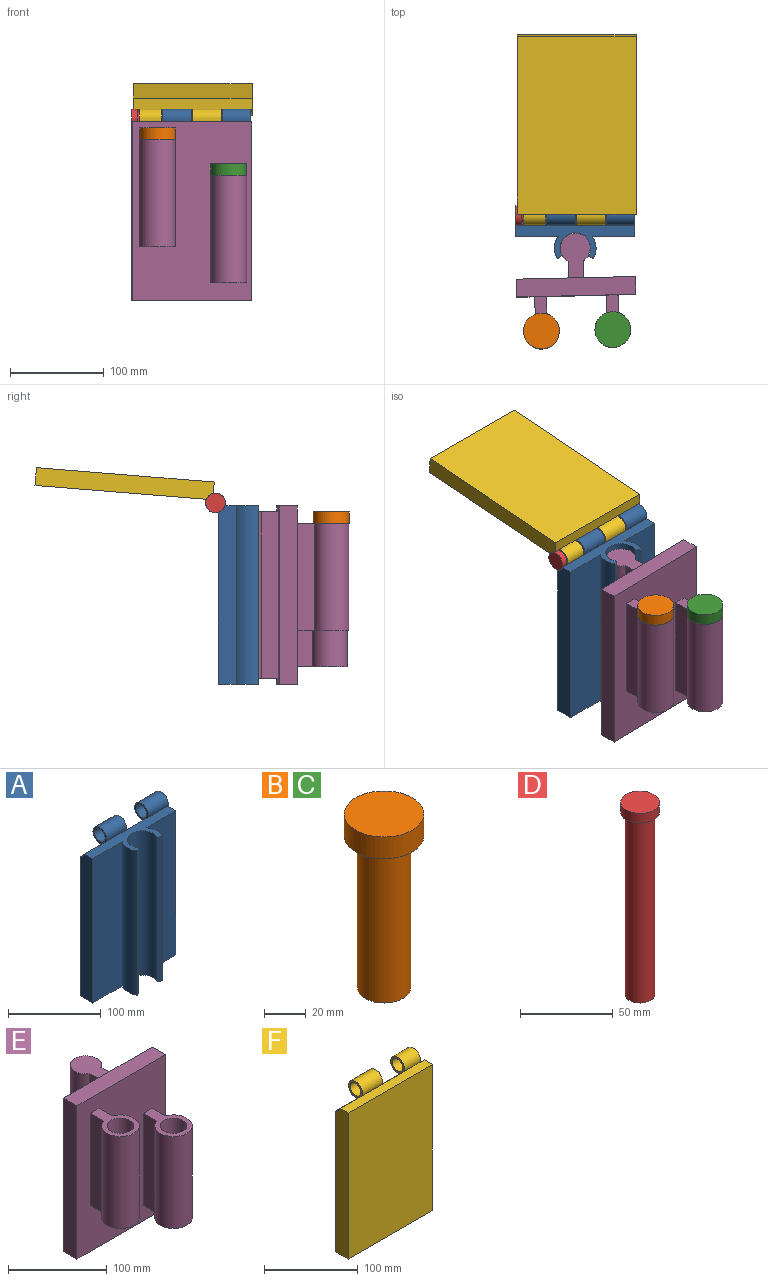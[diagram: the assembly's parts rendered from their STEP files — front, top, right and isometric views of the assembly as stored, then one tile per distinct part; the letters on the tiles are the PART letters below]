
ASSEMBLY  parts=6 mates=7
PART A: 21 faces, bbox 127x56.5x204.2 mm
  f0: cylinder r=10.48mm len=33.27mm, axis (1,0,0), area 333mm2, adj f3,f7,f17,f20
  f1: plane 190.5x45.26mm, normal (0,-1,0), area 8622.2mm2, adj f3,f4,f5,f10
  f2: plane 190.5x45.26mm, normal (0,-1,0), area 8622.2mm2, adj f3,f5,f6,f8
  f3: plane 127x36.05mm, normal (0,0,1), area 1790.7mm2, adj f0,f1,f2,f4,f6,f8,f9,f10
  f4: plane 190.5x19.05mm, normal (-1,0,0), area 3598.2mm2, adj f1,f3,f5,f7,f13
  f5: plane 127x42.86mm, normal (0,0,-1), area 2655.5mm2, adj f1,f2,f4,f6,f7,f8,f9,f10
  f6: plane 204.15x32.7mm, normal (1,0,0), area 3742mm2, adj f2,f3,f5,f7,f18,f19
  f7: plane 183.69x127mm, normal (0,1,0), area 23328.6mm2, adj f0,f4,f5,f6,f13,f15,f19
  f8: cylinder r=22.23mm len=190.5mm, axis (0,0,-1), area 4792.1mm2, adj f2,f3,f5,f9
  f9: plane 190.5x5.16mm, normal (-0.5,-0.87,0), area 1134.1mm2, adj f3,f5,f8,f12
  f10: cylinder r=22.23mm len=190.5mm, axis (0,0,-1), area 4792.1mm2, adj f1,f3,f5,f11
  f11: plane 190.5x5.16mm, normal (0.5,-0.87,0), area 1134.1mm2, adj f3,f5,f10,f12
  f12: cylinder r=16.27mm len=190.5mm, axis (0,0,-1), area 12984.4mm2, adj f3,f5,f9,f11
  f13: cylinder r=10.48mm len=33.27mm, axis (1,0,0), area 333mm2, adj f3,f4,f7,f16
  f14: cylinder r=8mm len=30.23mm, axis (1,0,0), area 1519.5mm2, adj f16,f17
  f15: cylinder r=10.48mm len=30.23mm, axis (1,0,0), area 1687.4mm2, adj f3,f7,f16,f17
  f16: plane 20.96x20.96mm, normal (-1,0,0), area 143.8mm2, adj f13,f14,f15
  f17: plane 20.96x20.96mm, normal (1,0,0), area 143.8mm2, adj f0,f14,f15
  f18: cylinder r=8mm len=30.23mm, axis (1,0,0), area 1519.5mm2, adj f6,f20
  f19: cylinder r=10.48mm len=30.23mm, axis (1,0,0), area 1687.4mm2, adj f3,f6,f7,f20
  f20: plane 20.96x20.96mm, normal (-1,0,0), area 143.8mm2, adj f0,f18,f19
PART B: 5 faces, bbox 38.1x38.1x101.6 mm
  f0: cylinder r=12.7mm len=88.9mm, axis (0,0,-1), area 7093.9mm2, adj f1,f4
  f1: plane 25.4x25.4mm, normal (0,0,-1), area 506.7mm2, adj f0
  f2: cylinder r=19.05mm len=38.1mm, axis (0,0,-1), area 1520.1mm2, adj f3,f4
  f3: plane 38.1x38.1mm, normal (0,0,1), area 1140.1mm2, adj f2
  f4: plane 38.1x38.1mm, normal (0,0,-1), area 633.4mm2, adj f0,f2
PART C: same geometry as B
PART D: 5 faces, bbox 21x21x127 mm
  f0: cylinder r=7.94mm len=120.65mm, axis (0,0,-1), area 6017.2mm2, adj f1,f4
  f1: plane 15.88x15.88mm, normal (0,0,-1), area 197.9mm2, adj f0
  f2: cylinder r=10.48mm len=20.96mm, axis (0,0,-1), area 418mm2, adj f3,f4
  f3: plane 20.96x20.96mm, normal (0,0,1), area 344.9mm2, adj f2
  f4: plane 20.96x20.96mm, normal (0,0,-1), area 146.9mm2, adj f0,f2
PART E: 23 faces, bbox 127x122.7x190.5 mm
  f0: plane 190.5x127mm, normal (0,-1,0), area 21290.3mm2, adj f1,f2,f3,f4,f7,f8,f10,f11
  f1: plane 190.5x19.05mm, normal (1,0,0), area 3629mm2, adj f0,f2,f4,f5
  f2: plane 127x19.05mm, normal (0,0,1), area 2419.3mm2, adj f0,f1,f3,f5
  f3: plane 190.5x19.05mm, normal (-1,0,0), area 3629mm2, adj f0,f2,f4,f5
  f4: plane 127x19.05mm, normal (0,0,-1), area 2419.3mm2, adj f0,f1,f3,f5
  f5: plane 190.5x127mm, normal (0,1,0), area 21370.9mm2, adj f1,f2,f3,f4,f18,f19,f21,f22
  f6: cylinder r=19.05mm len=114.3mm, axis (0,0,-1), area 12201.2mm2, adj f7,f8,f10,f11
  f7: plane 114.3x19.05mm, normal (1,0,0), area 2177.4mm2, adj f0,f6,f10,f11
  f8: plane 114.3x19.05mm, normal (-1,0,0), area 2177.4mm2, adj f0,f6,f10,f11
  f9: cylinder r=13.46mm len=114.3mm, axis (0,0,-1), area 9668mm2, adj f10,f11
  f10: plane 56.06x38.1mm, normal (0,0,1), area 803.4mm2, adj f0,f6,f7,f8,f9
  f11: plane 56.06x38.1mm, normal (0,0,-1), area 803.4mm2, adj f0,f6,f7,f8,f9
  f12: plane 114.3x19.05mm, normal (-1,0,0), area 2177.4mm2, adj f0,f13,f16,f17
  f13: cylinder r=19.05mm len=114.3mm, axis (0,0,-1), area 12201.2mm2, adj f12,f14,f16,f17
  f14: plane 114.3x19.05mm, normal (1,0,0), area 2177.4mm2, adj f0,f13,f16,f17
  f15: cylinder r=13.46mm len=114.3mm, axis (0,0,-1), area 9668mm2, adj f16,f17
  f16: plane 56.06x38.1mm, normal (0,0,1), area 803.4mm2, adj f0,f12,f13,f14,f15
  f17: plane 56.06x38.1mm, normal (0,0,-1), area 803.4mm2, adj f0,f12,f13,f14,f15
  f18: plane 177.8x18mm, normal (-1,0,0), area 3200.7mm2, adj f5,f20,f21,f22
  f19: plane 177.8x18mm, normal (1,0,0), area 3200.7mm2, adj f5,f20,f21,f22
  f20: cylinder r=15.88mm len=177.8mm, axis (0,0,-1), area 14779mm2, adj f18,f19,f21,f22
  f21: plane 47.63x31.75mm, normal (0,0,1), area 1054.7mm2, adj f5,f18,f19,f20
  f22: plane 47.63x31.75mm, normal (0,0,-1), area 1054.7mm2, adj f5,f18,f19,f20
PART F: 17 faces, bbox 127x32.7x204.2 mm
  f0: cylinder r=10.48mm len=33.27mm, axis (1,0,0), area 333mm2, adj f1,f6,f11,f14
  f1: plane 127x12.24mm, normal (0,0,1), area 1554.5mm2, adj f0,f2,f4,f5,f7,f9,f13,f15
  f2: plane 190.5x19.05mm, normal (-1,0,0), area 3598.2mm2, adj f1,f3,f5,f6,f7
  f3: plane 127x19.05mm, normal (0,0,-1), area 2419.3mm2, adj f2,f4,f5,f6
  f4: plane 190.5x19.05mm, normal (1,0,0), area 3598.2mm2, adj f1,f3,f5,f6,f15
  f5: plane 190.5x127mm, normal (0,-1,0), area 24193.5mm2, adj f1,f2,f3,f4
  f6: plane 183.69x127mm, normal (0,1,0), area 23328.6mm2, adj f0,f2,f3,f4,f7,f9,f13,f15
  f7: cylinder r=10.48mm len=33.27mm, axis (1,0,0), area 333mm2, adj f1,f2,f6,f10
  f8: cylinder r=8mm len=30.23mm, axis (1,0,0), area 1519.5mm2, adj f10,f11
  f9: cylinder r=10.48mm len=30.23mm, axis (1,0,0), area 1687.4mm2, adj f1,f6,f10,f11
  f10: plane 20.96x20.96mm, normal (-1,0,0), area 143.8mm2, adj f7,f8,f9
  f11: plane 20.96x20.96mm, normal (1,0,0), area 143.8mm2, adj f0,f8,f9
  f12: cylinder r=8mm len=23.88mm, axis (1,0,0), area 1200.3mm2, adj f14,f16
  f13: cylinder r=10.48mm len=23.88mm, axis (1,0,0), area 1332.9mm2, adj f1,f6,f14,f16
  f14: plane 20.96x20.96mm, normal (-1,0,0), area 143.8mm2, adj f0,f12,f13
  f15: cylinder r=10.48mm len=6.81mm, axis (1,0,0), area 63.5mm2, adj f1,f4,f6,f16
  f16: plane 20.96x20.96mm, normal (1,0,0), area 143.8mm2, adj f12,f13,f15
PLACE A t=(0,22.22,0)mm
PLACE B rot(axis=(0,0,-1),88.7deg) t=(-36.12,-88.64,31.75)mm
PLACE C rot(axis=(0,0,1),11.9deg) t=(40.06,-86.93,-6.35)mm
PLACE D rot(axis=(0.29,-0.91,-0.29),95.3deg) t=(3.17,34.93,98.43)mm
PLACE E rot(axis=(0,0,1),1.3deg) t=(0.93,-41.26,0)mm
PLACE F rot(axis=(0,0.74,-0.68),180deg) t=(1.52,132,119.02)mm
MATE fastened B.f2 <-> E.f6  axis (0,0,-1) through (-36.12,-88.64,76.2)mm
MATE revolute F.f15 <-> A.f18  axis (-1,0,0) through (16.64,34.93,98.43)mm
MATE cylindrical E.f13 <-> C.f0  axis (0,0,1) through (40.06,-86.93,38.1)mm
MATE cylindrical E.f6 <-> B.f0  axis (0,0,1) through (-36.12,-88.64,76.2)mm
MATE revolute E.f20 <-> A.f12  axis (0,0,-1) through (0,0,0)mm
MATE cylindrical D.f0 <-> A.f18  axis (1,0,0) through (3.17,34.93,98.43)mm
MATE planar E.f13 <-> C.f0  axis (0,0,-1) through (40.06,-86.93,38.1)mm
